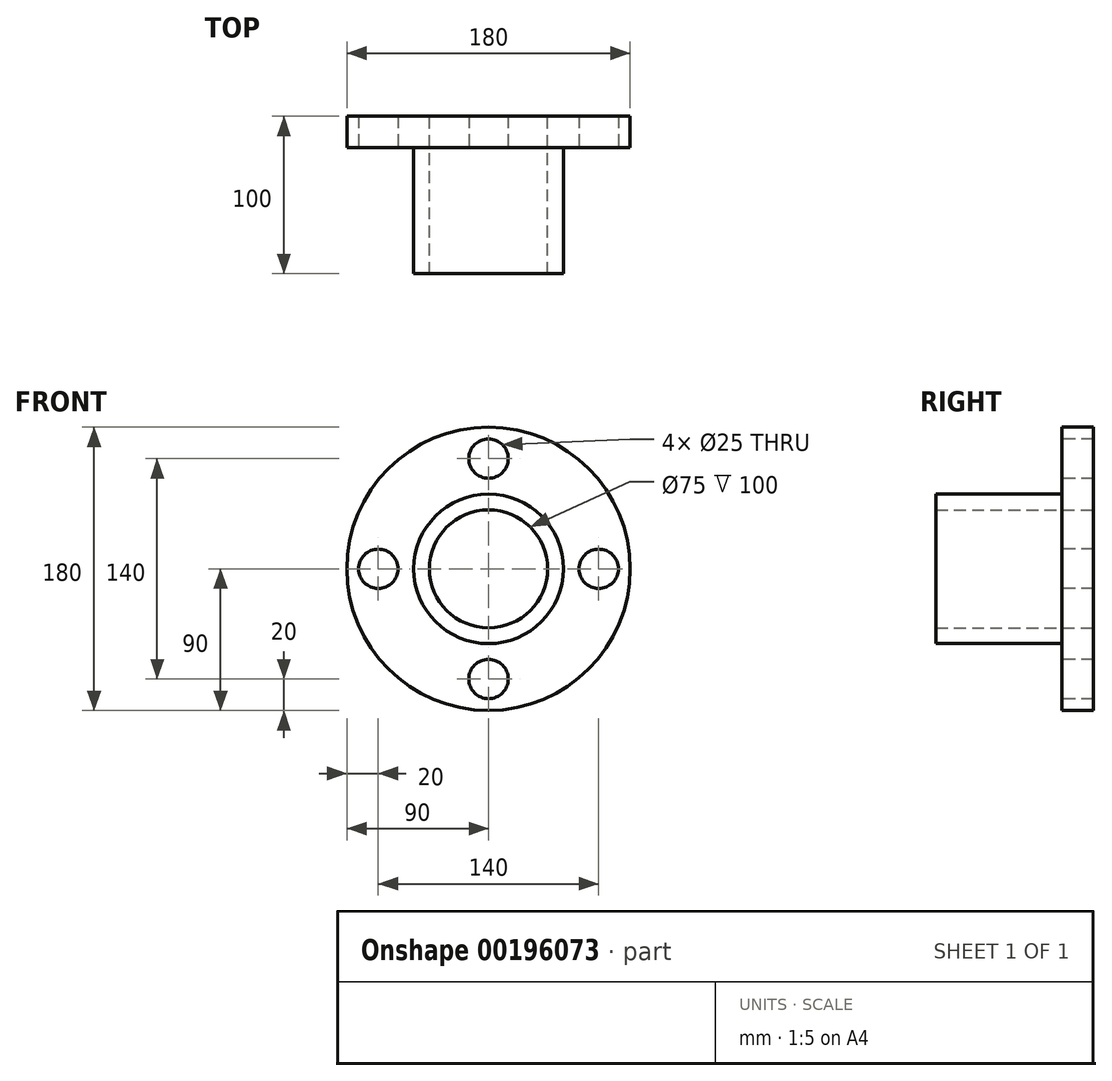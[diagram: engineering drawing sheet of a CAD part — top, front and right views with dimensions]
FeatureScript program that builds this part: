
annotation { "Feature Type Name" : "Feature", "Feature Type Description" : "" }
export const myFeature = defineFeature(function(context is Context, id is Id, definition is map)
    precondition{}
    {
        {
            var Q0;
            Q0=qCreatedBy(makeId("Right.planeOp"),FACE);
            var sketch = newSketch(context, id + "F0", { "sketchPlane" : qUnion([Q0])});
            skLineSegment(sketch, "E0", {"start": v(0, 0) * mm, "end": v(-106.62, 0) * mm, "construction": true});
            skLineSegment(sketch, "E1.bottom", {"start": v(0, 37.5) * mm, "end": v(-100, 37.5) * mm});
            skLineSegment(sketch, "E1.top", {"start": v(0, 90) * mm, "end": v(-20, 90) * mm});
            skLineSegment(sketch, "E1.left", {"start": v(0, 37.5) * mm, "end": v(0, 90) * mm});
            skLineSegment(sketch, "E1.right", {"start": v(-100, 37.5) * mm, "end": v(-100, 47.5) * mm});
            skLineSegment(sketch, "E2.top", {"start": v(-100, 47.5) * mm, "end": v(-20, 47.5) * mm});
            skLineSegment(sketch, "E2.right", {"start": v(-20, 90) * mm, "end": v(-20, 47.5) * mm});
            skSolve(sketch);
        }
        {
            var Q0;
            Q0 = qSketchRegion(id + "F0", true);
            var Q1;
            Q1=sQuery(id+"F0.wireOp",EDGE,"E0");
            revolve(context, id + "F1", {"entities" : qUnion([Q0]), "axis" : qUnion([Q1]), "revolveType" : RevolveType.FULL});
        }
        {
            var Q0;
            Q0=makeQuery(id+"F1.opRevolve","SWEPT_FACE",FACE,{"disambiguationData":[OSD([sQuery(id+"F0.wireOp",EDGE,"E2.right")])]});
            var sketch = newSketch(context, id + "F2", { "sketchPlane" : qUnion([Q0])});
            skCircle(sketch, "E3", {"center": v(0, 70) * mm, "radius": 12.5 * mm});
            skSolve(sketch);
        }
        {
            var Q0;
            Q0 = qSketchRegion(id + "F2", true);
            extrude(context, id + "F3", {"entities" : qUnion([Q0]), "operationType" : NewBodyOperationType.REMOVE, "endBound" : BoundingType.THROUGH_ALL, "oppositeDirection" : true, "depth" : 25 * mm});
        }
        {
            var Q0;
            Q0=makeQuery(id+"F3.boolean.opBoolean","COPY",FACE,{"derivedFrom":makeQuery(id+"F3.opExtrude","SWEPT_FACE",FACE,{"disambiguationData":[OSD([sQuery(id+"F2.wireOp",EDGE,"E3")])]})});
            var Q1;
            Q1=makeQuery(id+"F1.opRevolve","SWEPT_FACE",FACE,{"disambiguationData":[OSD([sQuery(id+"F0.wireOp",EDGE,"E1.bottom")])]});
            circularPattern(context, id + "F4", {"patternType" : PatternType.FACE, "faces" : qUnion([Q0]), "axis" : qUnion([Q1]), "angle" : 360 * degree, "instanceCount" : 4, "equalSpace" : true});
        }
    });
